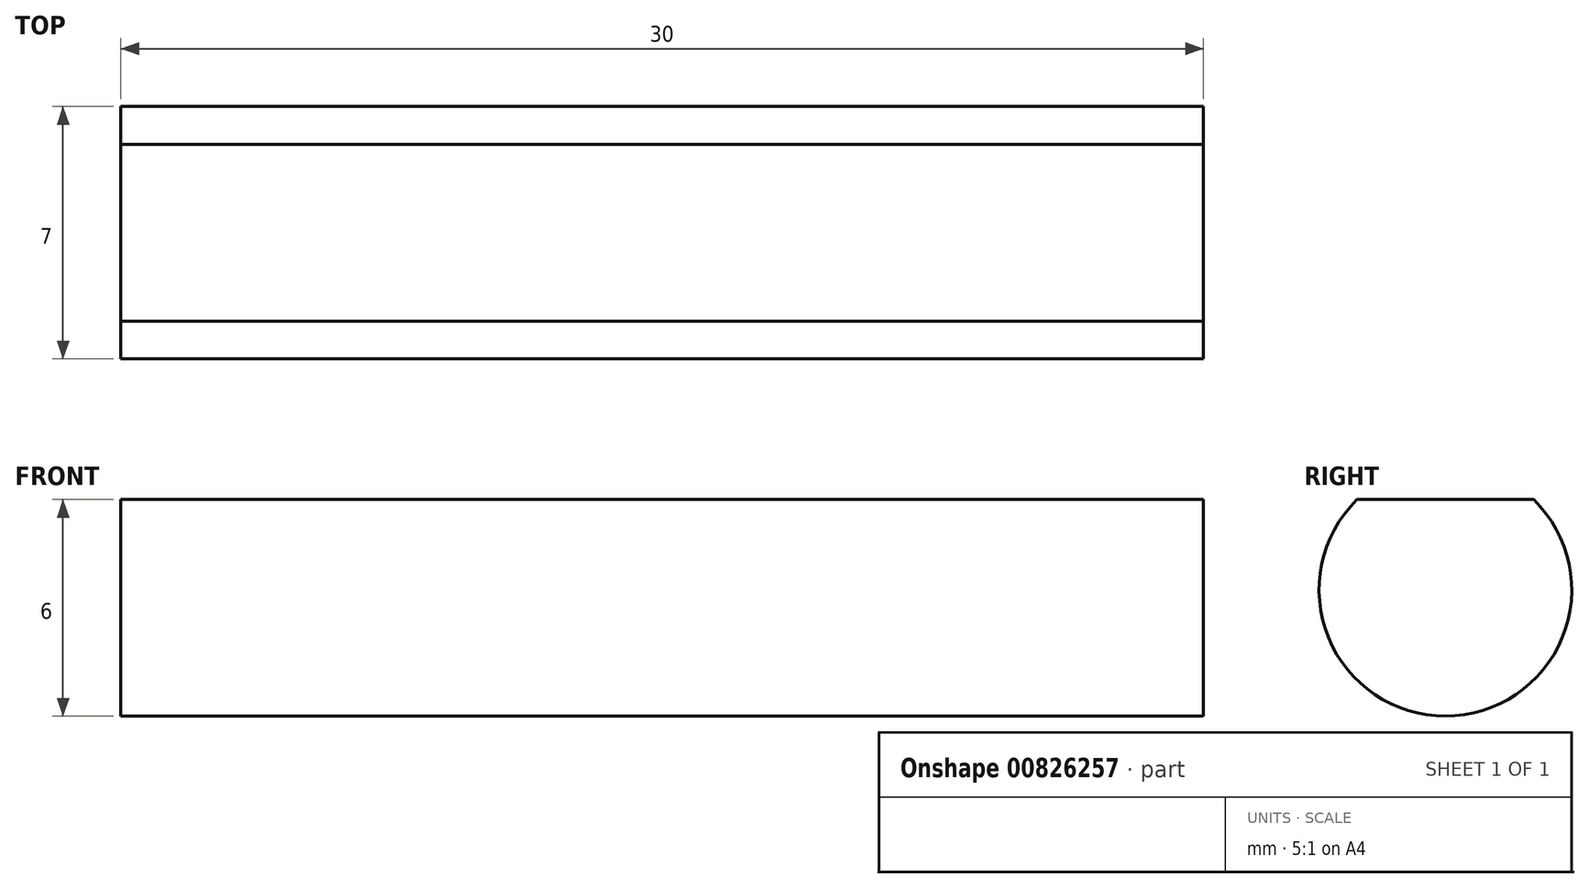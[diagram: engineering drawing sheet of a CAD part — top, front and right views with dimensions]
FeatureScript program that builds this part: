
annotation { "Feature Type Name" : "Feature", "Feature Type Description" : "" }
export const myFeature = defineFeature(function(context is Context, id is Id, definition is map)
    precondition{}
    {
        {
            var Q0;
            Q0=qCreatedBy(makeId("Right.planeOp"),FACE);
            var sketch = newSketch(context, id + "F0", { "sketchPlane" : qUnion([Q0])});
            skCircle(sketch, "E0", {"center": v(0, 0) * mm, "radius": 3.5 * mm});
            skLineSegment(sketch, "E1", {"start": v(0, 0) * mm, "end": v(0, 3.5) * mm});
            skLineSegment(sketch, "E2", {"start": v(0, 0) * mm, "end": v(0, -3.5) * mm});
            skLineSegment(sketch, "E3", {"start": v(0, 2.5) * mm, "end": v(-2.45, 2.5) * mm});
            skLineSegment(sketch, "E4", {"start": v(0, 2.5) * mm, "end": v(2.45, 2.5) * mm});
            skSolve(sketch);
        }
        {
            var Q0;
            {var subQ0=sQuery(id+"F0.wireOp",EDGE,"E2");Q0=makeQuery(id+"F0.imprint","IMPRINT",FACE,{"disambiguationData":[TD([[makeQuery(id+"F0.imprint","IMPRINT",EDGE,{"derivedFrom":subQ0}),-1.0]])]});}
            var Q1;
            {var subQ0=sQuery(id+"F0.wireOp",EDGE,"E2");Q1=makeQuery(id+"F0.imprint","IMPRINT",FACE,{"disambiguationData":[TD([[makeQuery(id+"F0.imprint","IMPRINT",EDGE,{"derivedFrom":subQ0}),1.0]])]});}
            extrude(context, id + "F1", {"entities" : qUnion([Q0, Q1]), "endBound" : BoundingType.SYMMETRIC, "depth" : 30 * mm, "offsetDistance" : 25 * mm});
        }
    });
